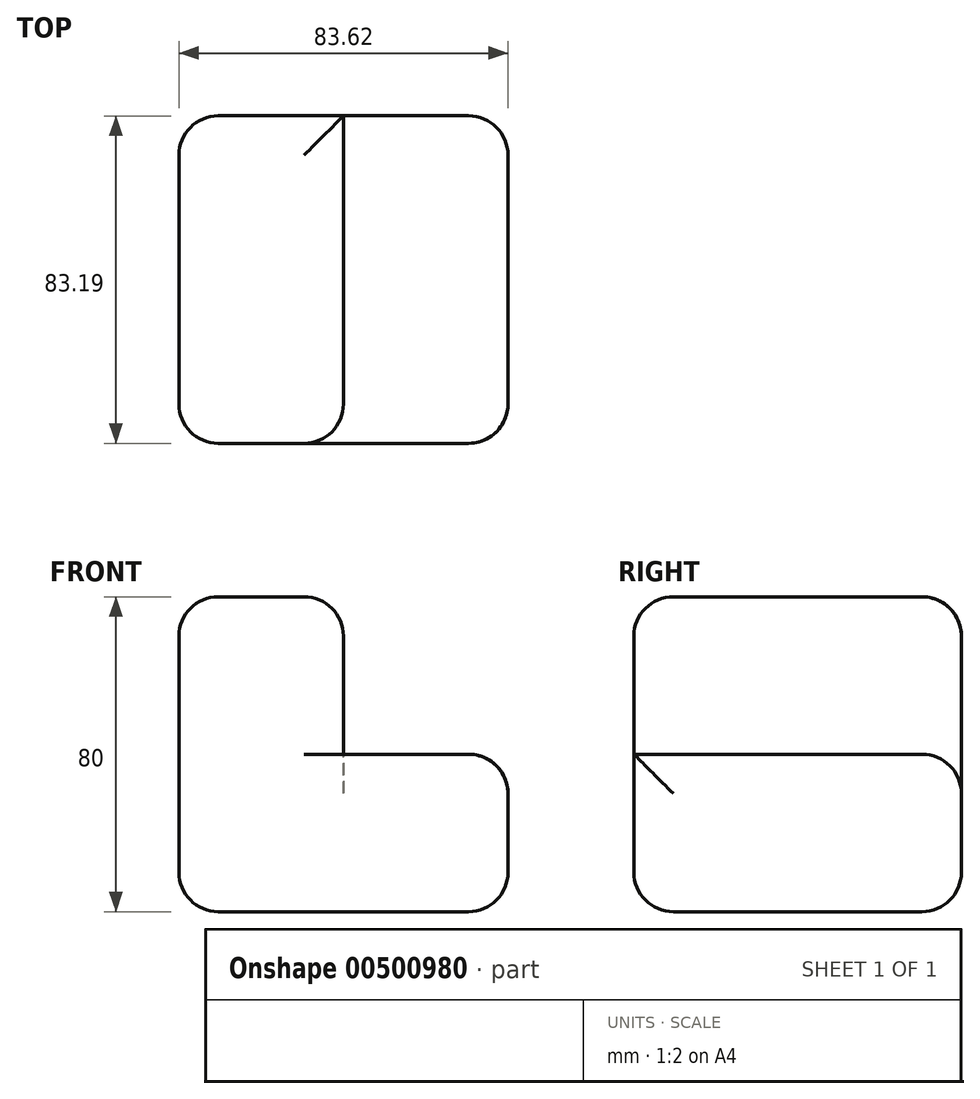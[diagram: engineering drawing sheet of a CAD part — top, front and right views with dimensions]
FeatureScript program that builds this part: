
annotation { "Feature Type Name" : "Feature", "Feature Type Description" : "" }
export const myFeature = defineFeature(function(context is Context, id is Id, definition is map)
    precondition{}
    {
        {
            var Q0;
            Q0=qCreatedBy(makeId("Top.planeOp"),FACE);
            var sketch = newSketch(context, id + "F0", { "sketchPlane" : qUnion([Q0])});
            skLineSegment(sketch, "E0.bottom", {"start": v(-59.13, -45.93) * mm, "end": v(24.5, -45.93) * mm});
            skLineSegment(sketch, "E0.top", {"start": v(-59.13, 37.26) * mm, "end": v(24.5, 37.26) * mm});
            skLineSegment(sketch, "E0.left", {"start": v(-59.13, -45.93) * mm, "end": v(-59.13, 37.26) * mm});
            skLineSegment(sketch, "E0.right", {"start": v(24.5, -45.93) * mm, "end": v(24.5, 37.26) * mm});
            skSolve(sketch);
        }
        {
            var Q0;
            Q0=makeQuery(id+"F0.imprint","IMPRINT",FACE,{"disambiguationData":[TD([[makeQuery(id+"F0.imprint","IMPRINT",EDGE,{"derivedFrom":sQuery(id+"F0.wireOp",EDGE,"E0.bottom")}),1.0]])]});
            extrude(context, id + "F1", {"entities" : qUnion([Q0]), "depth" : 40 * mm});
        }
        {
            var Q0;
            Q0=makeQuery(id+"F1.opExtrude","CAP_FACE",FACE,{"disambiguationData":[OSD([sQuery(id+"F0.wireOp",EDGE,"E0.bottom"),sQuery(id+"F0.wireOp",EDGE,"E0.top"),sQuery(id+"F0.wireOp",EDGE,"E0.left"),sQuery(id+"F0.wireOp",EDGE,"E0.right")])],"isStart":false});
            var sketch = newSketch(context, id + "F2", { "sketchPlane" : qUnion([Q0])});
            skLineSegment(sketch, "E1", {"start": v(-17.32, 37.26) * mm, "end": v(-17.32, -45.93) * mm});
            skSolve(sketch);
        }
        {
            var Q0;
            {var subQ1=sQuery(id+"F2.wireOp",EDGE,"E1");Q0=makeQuery(id+"F2.imprint","IMPRINT",FACE,{"disambiguationData":[TD([[makeQuery(id+"F2.imprint","IMPRINT",EDGE,{"derivedFrom":subQ1}),-1.0]])]});}
            extrude(context, id + "F3", {"entities" : qUnion([Q0]), "operationType" : NewBodyOperationType.ADD, "depth" : 40 * mm});
        }
        {
            var Q0;
            Q0=makeQuery(id+"F3.opExtrude","CAP_EDGE",EDGE,{"disambiguationData":[OSD([sQuery(id+"F2.wireOp",EDGE,"E1")])],"isStart":true});
            var Q1;
            Q1=makeQuery(id+"F3.opExtrude","CAP_EDGE",EDGE,{"disambiguationData":[OSD([sQuery(id+"F2.wireOp",EDGE,"E1")])],"isStart":false});
            var Q2;
            Q2=makeQuery(id+"F3.opExtrude","CAP_EDGE",EDGE,{"disambiguationData":[OSD([sQuery(id+"F0.wireOp",EDGE,"E0.bottom")])],"isStart":false});
            var Q3;
            Q3=makeQuery(id+"F3.opExtrude","SWEPT_EDGE",EDGE,{"disambiguationData":[OSD([sQuery(id+"F0.wireOp",EDGE,"E0.bottom"),sQuery(id+"F2.wireOp",EDGE,"E1")])]});
            var Q4;
            Q4=makeQuery(id+"F3.opExtrude","CAP_EDGE",EDGE,{"disambiguationData":[OSD([sQuery(id+"F0.wireOp",EDGE,"E0.left")])],"isStart":false});
            var Q5;
            Q5=makeQuery(id+"F3.opExtrude","CAP_EDGE",EDGE,{"disambiguationData":[OSD([sQuery(id+"F0.wireOp",EDGE,"E0.top")])],"isStart":false});
            var Q6;
            Q6=makeQuery(id+"F1.opExtrude","CAP_EDGE",EDGE,{"disambiguationData":[OSD([sQuery(id+"F0.wireOp",EDGE,"E0.top")])],"isStart":false});
            var Q7;
            Q7=makeQuery(id+"F1.opExtrude","CAP_EDGE",EDGE,{"disambiguationData":[OSD([sQuery(id+"F0.wireOp",EDGE,"E0.right")])],"isStart":false});
            var Q8;
            Q8=makeQuery(id+"F1.opExtrude","SWEPT_EDGE",EDGE,{"disambiguationData":[OSD([sQuery(id+"F0.wireOp",EDGE,"E0.bottom"),sQuery(id+"F0.wireOp",EDGE,"E0.right")])]});
            var Q9;
            Q9=makeQuery(id+"F1.opExtrude","SWEPT_EDGE",EDGE,{"disambiguationData":[OSD([sQuery(id+"F0.wireOp",EDGE,"E0.top"),sQuery(id+"F0.wireOp",EDGE,"E0.right")])]});
            var Q10;
            Q10=makeQuery(id+"F1.opExtrude","CAP_EDGE",EDGE,{"disambiguationData":[OSD([sQuery(id+"F0.wireOp",EDGE,"E0.bottom")])],"isStart":true});
            var Q11;
            {var subQ0=sQuery(id+"F0.wireOp",EDGE,"E0.left");var subQ1=sQuery(id+"F0.wireOp",EDGE,"E0.bottom");Q11=makeQuery(id+"F3.boolean.opBoolean","MERGE",EDGE,{"derivedFrom":[makeQuery(id+"F1.opExtrude","SWEPT_EDGE",EDGE,{"disambiguationData":[OSD([subQ1,subQ0])]}),makeQuery(id+"F3.opExtrude","SWEPT_EDGE",EDGE,{"disambiguationData":[OSD([subQ1,subQ0])]})]});}
            var Q12;
            {var subQ0=sQuery(id+"F0.wireOp",EDGE,"E0.left");var subQ1=sQuery(id+"F0.wireOp",EDGE,"E0.top");Q12=makeQuery(id+"F3.boolean.opBoolean","MERGE",EDGE,{"derivedFrom":[makeQuery(id+"F1.opExtrude","SWEPT_EDGE",EDGE,{"disambiguationData":[OSD([subQ1,subQ0])]}),makeQuery(id+"F3.opExtrude","SWEPT_EDGE",EDGE,{"disambiguationData":[OSD([subQ1,subQ0])]})]});}
            var Q13;
            Q13=makeQuery(id+"F1.opExtrude","CAP_EDGE",EDGE,{"disambiguationData":[OSD([sQuery(id+"F0.wireOp",EDGE,"E0.left")])],"isStart":true});
            var Q14;
            Q14=makeQuery(id+"F1.opExtrude","CAP_EDGE",EDGE,{"disambiguationData":[OSD([sQuery(id+"F0.wireOp",EDGE,"E0.top")])],"isStart":true});
            var Q15;
            Q15=makeQuery(id+"F1.opExtrude","CAP_EDGE",EDGE,{"disambiguationData":[OSD([sQuery(id+"F0.wireOp",EDGE,"E0.right")])],"isStart":true});
            fillet(context, id + "F4", {"entities" : qUnion([Q0, Q1, Q2, Q3, Q4, Q5, Q6, Q7, Q8, Q9, Q10, Q11, Q12, Q13, Q14, Q15]), "radius" : 10 * mm, "tangentPropagation" : true, "allowEdgeOverflow" : false});
        }
    });
